# Revit family: LWplc_Latchwaysplc_BaluAndGuardSym_VersiRail_Freestanding
name_source: partatom
category: Railings
revit_build: Autodesk Revit 2013 (Build: 20121003_2115(x64)
units: mm (PartAtom-declared; Revit-internal decimal feet)

## types (3) — shared parameters
AssetType = Movable
BasePlateMaterial = LWplc_Latchwaysplc_Aluminium_Polished
CounterWeightMaterial = LWplc_Latchwaysplc_Plastic_VersiRailWeight
Default Elevation = 1219 mm
Description = Latchways ManSafe® for Roofing, using VersiRail
Diameter = 40 mm  [stored 0.131234 ft]
DurationUnit = year
Height = 1150 mm
IfcExportAs = GUARDRAIL
IfcExportType = IfcRailing
IsExternal = Yes
ManufacturerName = Latchways plc
ManufacturerURL = www.latchways.com
Material = Handrails & Uprights: Aluminium; Counterweight: Concrete filled HDPE with UV protection
Model = 22100-00+22080-00
NBSDescription = Balustrade and guarding system
NBSReference = 25-25-10/110
NominalHeight = 1150 mm
NominalLength = 1310 mm  [stored 4.2979 ft]
NominalWidth = 253 mm  [stored 0.830052 ft]
RailAngle = 90.00°
RailMaterial = LWplc_Latchwaysplc_Aluminium_Polished
Size = 235 x 1310 x 1150 mm
URL = www.latchways.com
Uniclass2 = Ss_25_15_60_05
Version = 1
WarrantyDurationUnit = year

## per-type parameters (varying)
| type | BIMObjectName | Curved | Inclined | ModelNumber | ModelReference | ProductInformation | Straight |
| BalustradeAndGuardingSystem_VersiRailFreestanding_Straight_Latchwaysplc | LWplc_Latchwaysplc_BalustradeAndGuardingSystem_VersiRailFreestanding_Straight | No | No | 22000-00+22080-01 | VersiRail - Straight Freestanding assembly | www.latchways.com/BIM/Latchways_FreestandingStraightVersiRail_Datasheet.pdf | Yes |
| BalustradeAndGuardingSystem_VersiRailFreestanding_Inclined_Latchwaysplc | LWplc_Latchwaysplc_BalustradeAndGuardingSystem_VersiRailFreestanding_Inclined | No | Yes | 22100-00+22080-01 | VersiRail - Inclined Freestanding assembly | www.latchways.com/BIM/Latchways_FreestandingInclinedVersiRail_Datasheet.pdf | No |
| BalustradeAndGuardingSystem_VersiRailFreestanding_Curved_Latchwaysplc | LWplc_Latchwaysplc_BalustradeAndGuardingSystem_VersiRailFreestanding_Curved | Yes | No | 22200-00+22080-01 | VersiRail - Curved Freestanding assembly | www.latchways.com/BIM/Latchways_FreestandingCurvedVersiRail_Datasheet.pdf | No |

note: column(s) folded — value = type name in every type: Name

note: [stored X ft] marks values corroborated as IEEE doubles in the binary element streams (Revit-internal decimal feet)

## geometry (parser evidence)
native form markers: Blend x8, Sweep x12
no freeform markers — native parametric forms only
